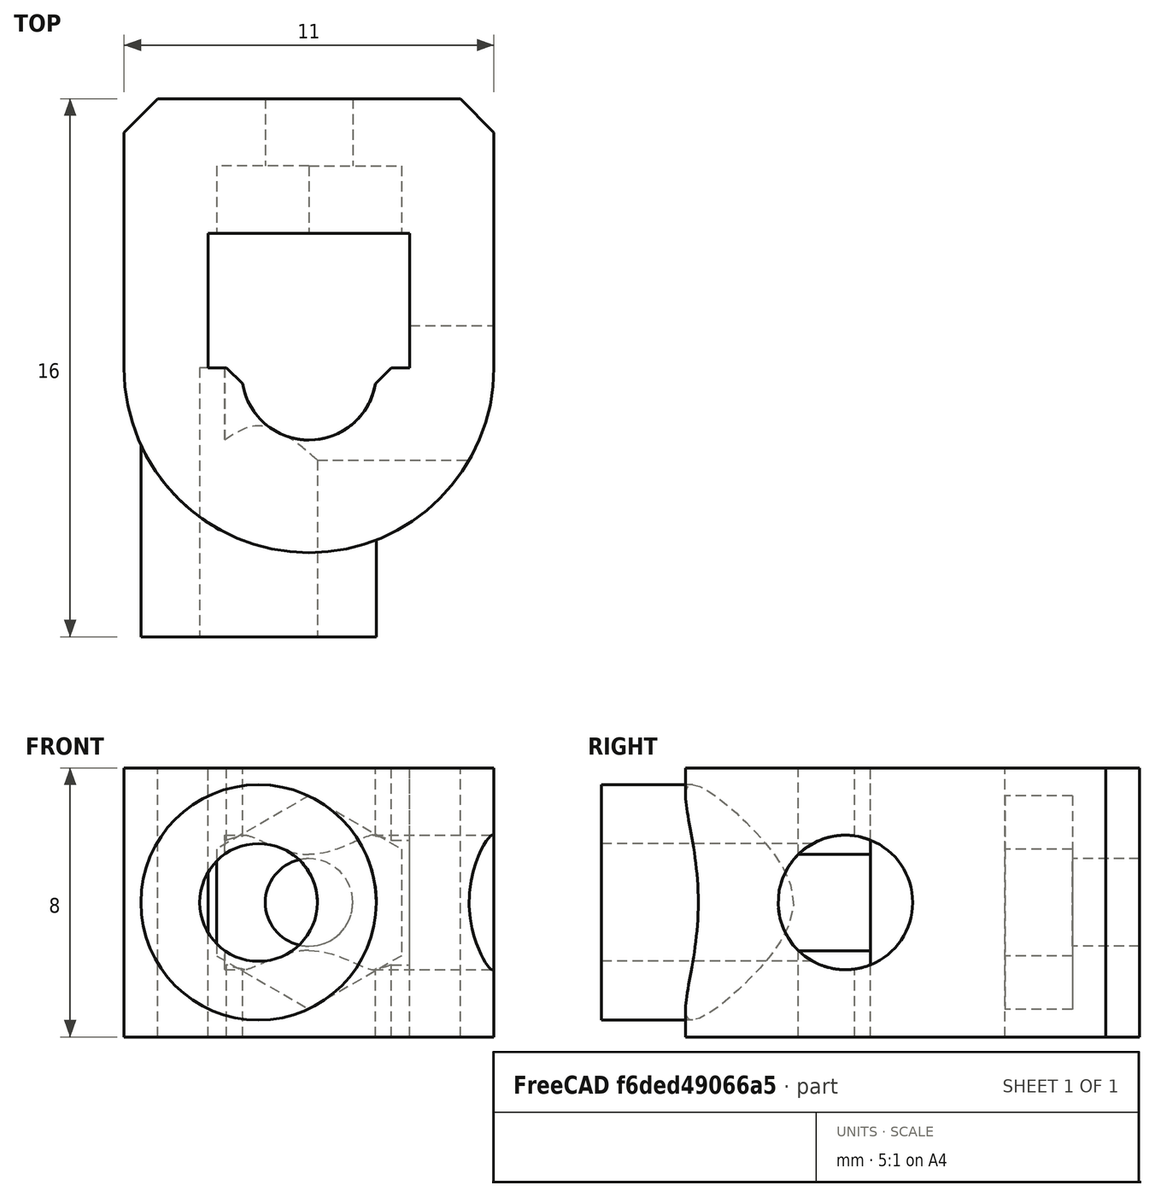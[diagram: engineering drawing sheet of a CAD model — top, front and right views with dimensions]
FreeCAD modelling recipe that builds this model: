
FCSTD DOCUMENT  (FreeCAD 0.14R2935 (Git))
Label: tendon_fastener_for_bolt_3mm
License: CC-BY 3.0
LicenseURL: http://creativecommons.org/licenses/by/3.0/
objects: Part::Cylinder×6, Part::Box×4, Part::MultiFuse×4, Part::Extrusion×1, Part::Mirroring×1, Part::Chamfer×1, Part::Cut×1
note: 18 computed .brp shape members not serialized (recipe doc carries the construction recipe); baked Part::Feature solids carry a one-line shape summary decoded from their .brp

FEATURE [Part::Cylinder] Cylinder
  Angle = 360
  Height = 8
  Radius = 5.5
FEATURE [Part::Box] Box  label="Cube"
  Height = 10
  Length = 6
  Placement = pos=(-3,0,-2) rot=(0,0,1;0rad)
  Width = 4
FEATURE [Part::Cylinder] Cylinder001
  Angle = 360
  Height = 10
  Placement = pos=(0,-0.15,-2) rot=(0,0,1;0rad)
  Radius = 2
FEATURE [Part::Cylinder] Cylinder002
  Angle = 360
  Height = 10
  Placement = pos=(-1.5,0,3) rot=(1,0,0;1.5708rad)
  Radius = 1.75
FEATURE [Part::Cylinder] Cylinder003
  Angle = 360
  Height = 8
  Placement = pos=(-1.5,0,4) rot=(1,0,0;1.5708rad)
  Radius = 3.5
FEATURE [Part::Cylinder] Cylinder004
  Angle = 360
  Height = 10
  Placement = pos=(-2.5,-0.75,3) rot=(0,1,0;1.5708rad)
  Radius = 2
FEATURE [Part::MultiFuse] Fusion001
  Placement = pos=(0,0,1) rot=(0,0,1;0rad)
  Shapes = -> [Cylinder001,Cylinder002,Cylinder004,Box]
FEATURE [Part::Box] Box001  label="Cube001"
  Height = 8
  Length = 11
  Placement = pos=(-5.5,0,0) rot=(0,0,1;0rad)
  Width = 8
FEATURE [Part::Cylinder] Cylinder005
  Angle = 360
  Height = 10
  Placement = pos=(0,10,4) rot=(1,0,0;1.5708rad)
  Radius = 1.3
FEATURE [Part::Extrusion] Extrude
  Dir = (0,0,2)
  Solid = true
FEATURE [Part::Mirroring] Part__Mirroring  label="Extrude (Mirror #1)"
  Base = (0,0,0)
  Normal = (1,0,0)
  Source = -> Extrude
FEATURE [Part::MultiFuse] Fusion002
  Placement = pos=(0,6,4) rot=(1,0,0;1.5708rad)
  Shapes = -> [Part__Mirroring,Extrude]
FEATURE [Part::Box] Box003  label="Cube003"
  Height = 50
  Length = 2
  Placement = pos=(-1.45,-1,-25) rot=(0,0,1;0.785398rad)
  Width = 2
FEATURE [Part::Box] Box002  label="Cube002"
  Height = 50
  Length = 2
  Placement = pos=(1.45,-1,-25) rot=(0,0,1;0.785398rad)
  Width = 2
FEATURE [Part::MultiFuse] Fusion003
  Shapes = -> [Fusion002,Box003,Fusion001,Box002,Cylinder005]
FEATURE [Part::Chamfer] Chamfer
  Base = -> Box001
  Edges = 2 edges r=1: [Edge3,Edge7]
FEATURE [Part::MultiFuse] Fusion
  Shapes = -> [Cylinder,Cylinder003,Chamfer]
FEATURE [Part::Cut] Cut
  Base = -> Fusion
  Tool = -> Fusion003
